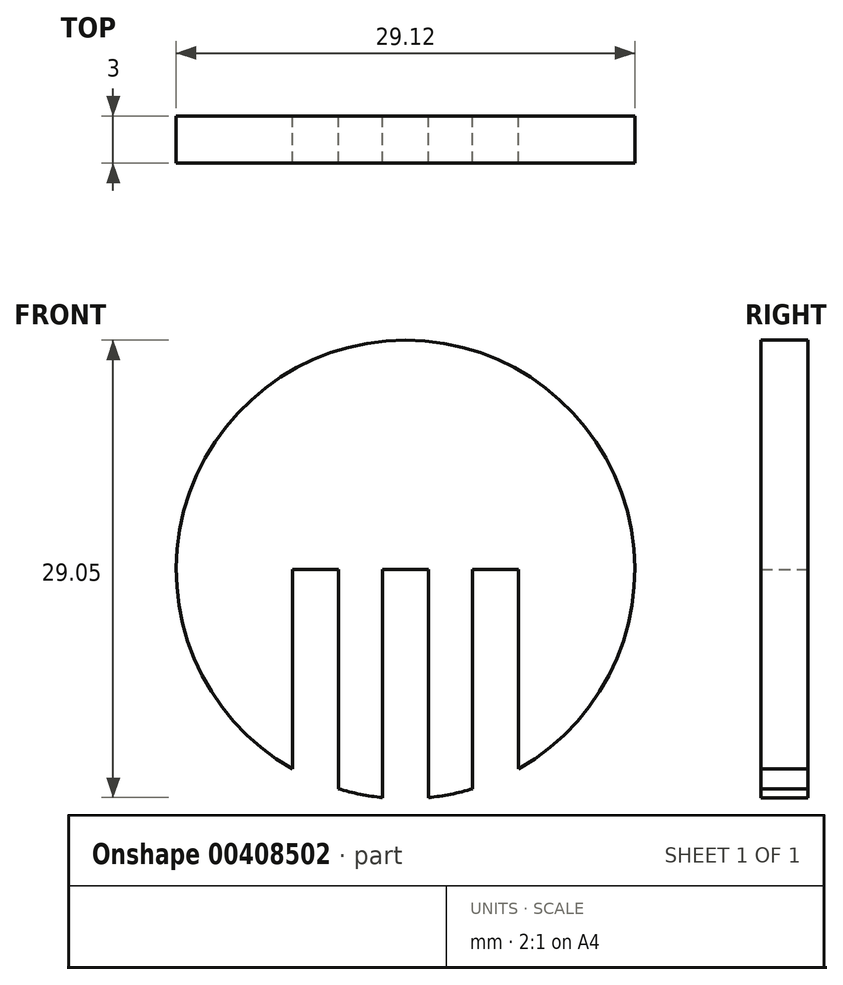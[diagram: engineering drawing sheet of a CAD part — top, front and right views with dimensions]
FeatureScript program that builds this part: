
annotation { "Feature Type Name" : "Feature", "Feature Type Description" : "" }
export const myFeature = defineFeature(function(context is Context, id is Id, definition is map)
    precondition{}
    {
        {
            var Q0;
            Q0=qCreatedBy(makeId("Front.planeOp"),FACE);
            var sketch = newSketch(context, id + "F0", { "sketchPlane" : qUnion([Q0])});
            skArc(sketch, "E0", {"start": v(0, 14.56) * mm, "mid": v(-14.09, 3.7) * mm, "end": v(-7.17, -12.68) * mm});
            skLineSegment(sketch, "E1.bottom", {"start": v(0, 0) * mm, "end": v(-1.45, 0) * mm});
            skLineSegment(sketch, "E1.right", {"start": v(-1.45, 0) * mm, "end": v(-1.45, -14.5) * mm});
            skLineSegment(sketch, "E2.bottom", {"start": v(-7.17, 0) * mm, "end": v(-4.27, 0) * mm});
            skLineSegment(sketch, "E2.left", {"start": v(-7.17, 0) * mm, "end": v(-7.17, -12.68) * mm});
            skLineSegment(sketch, "E2.right", {"start": v(-4.27, 0) * mm, "end": v(-4.27, -13.93) * mm});
            skArc(sketch, "E3.trimOffspring", {"start": v(-4.27, -13.93) * mm, "mid": v(-2.87, -14.28) * mm, "end": v(-1.45, -14.5) * mm});
            skLineSegment(sketch, "E4.MirrorCS", {"start": v(0, 0) * mm, "end": v(1.45, 0) * mm});
            skArc(sketch, "E5.MirrorCS", {"start": v(4.27, -13.93) * mm, "mid": v(2.87, -14.28) * mm, "end": v(1.45, -14.5) * mm});
            skLineSegment(sketch, "E6.MirrorCS", {"start": v(4.27, 0) * mm, "end": v(4.27, -13.93) * mm});
            skLineSegment(sketch, "E7.MirrorCS", {"start": v(1.45, 0) * mm, "end": v(1.45, -14.5) * mm});
            skArc(sketch, "E8.MirrorCS", {"start": v(0, 14.56) * mm, "mid": v(14.09, 3.7) * mm, "end": v(7.17, -12.68) * mm});
            skLineSegment(sketch, "E9.MirrorCS", {"start": v(7.17, 0) * mm, "end": v(7.17, -12.68) * mm});
            skLineSegment(sketch, "E10.MirrorCS", {"start": v(7.17, 0) * mm, "end": v(4.27, 0) * mm});
            skPoint(sketch, "E11.MirrorCS.end.orphan", {"position": v(0, -14.56) * mm});
            skSolve(sketch);
        }
        {
            var Q0;
            Q0 = qSketchRegion(id + "F0", true);
            var Q1;
            Q1=makeQuery(id+"F0.imprint","IMPRINT",FACE,{"disambiguationData":[TD([[makeQuery(id+"F0.imprint","IMPRINT",EDGE,{"derivedFrom":sQuery(id+"F0.wireOp",EDGE,"E0")}),1.0]])]});
            extrude(context, id + "F1", {"entities" : qUnion([Q0, Q1]), "depth" : 3 * mm});
        }
    });
